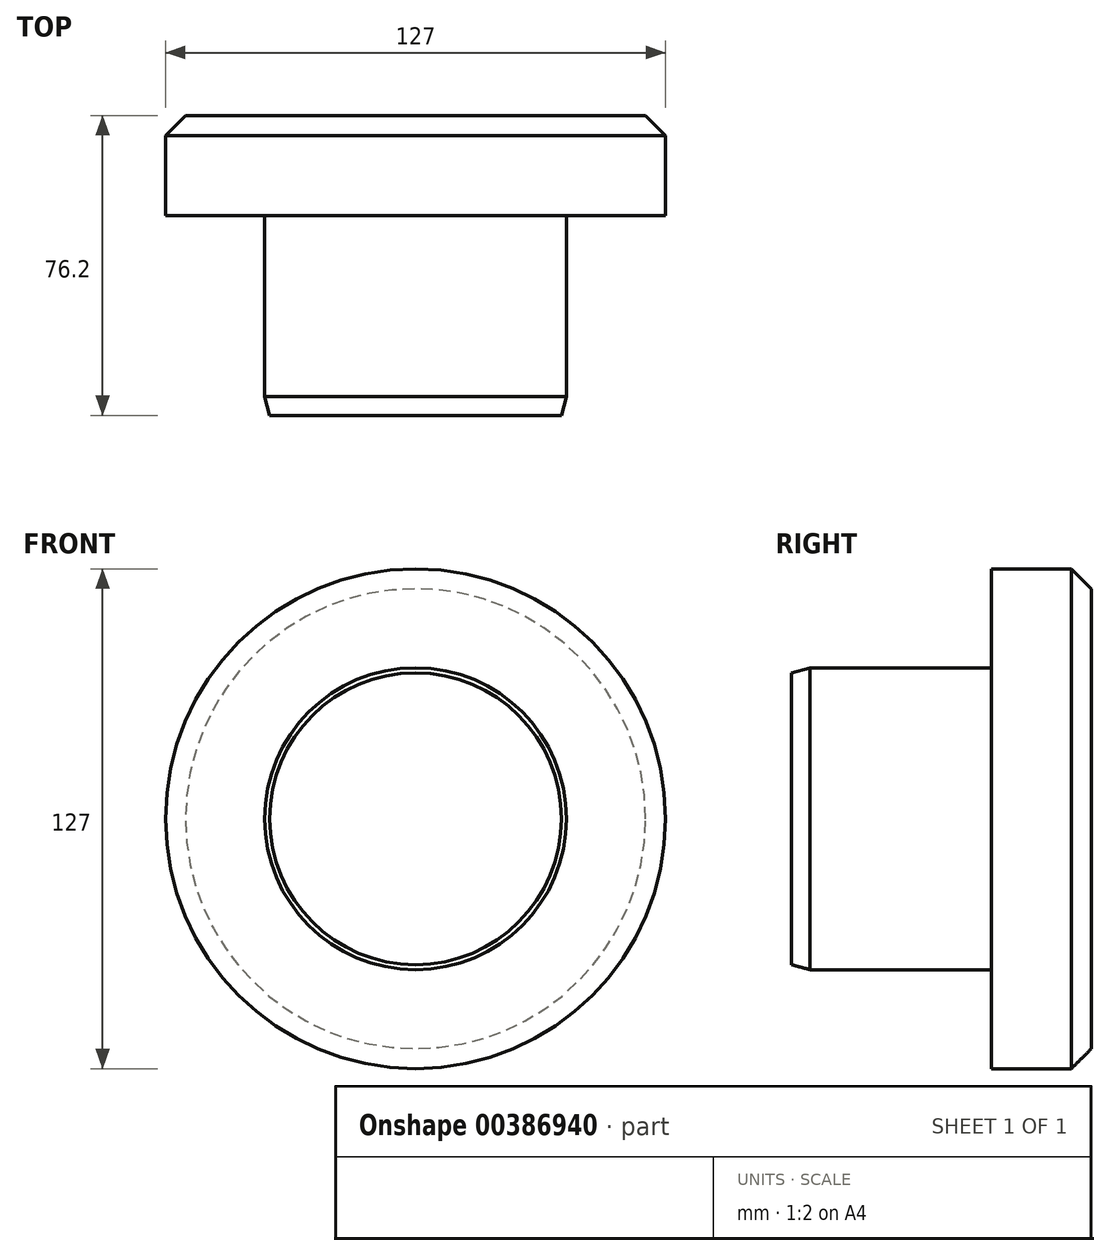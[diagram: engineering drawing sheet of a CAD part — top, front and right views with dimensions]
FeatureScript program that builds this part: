
annotation { "Feature Type Name" : "Feature", "Feature Type Description" : "" }
export const myFeature = defineFeature(function(context is Context, id is Id, definition is map)
    precondition{}
    {
        {
            var Q0;
            Q0=qCreatedBy(makeId("Front.planeOp"),FACE);
            var sketch = newSketch(context, id + "F0", { "sketchPlane" : qUnion([Q0])});
            skCircle(sketch, "E0", {"center": v(0, 0) * mm, "radius": 63.5 * mm});
            skSolve(sketch);
        }
        {
            var Q0;
            Q0 = qSketchRegion(id + "F0", true);
            extrude(context, id + "F1", {"entities" : qUnion([Q0]), "depth" : 76.2 * mm});
        }
        {
            var Q0;
            Q0=makeQuery(id+"F1.opExtrude","CAP_FACE",FACE,{"disambiguationData":[OSD([sQuery(id+"F0.wireOp",EDGE,"E0")])],"isStart":false});
            var sketch = newSketch(context, id + "F2", { "sketchPlane" : qUnion([Q0])});
            skCircle(sketch, "E1", {"center": v(0, 0) * mm, "radius": 38.35 * mm});
            skSolve(sketch);
        }
        {
            var Q0;
            Q0=makeQuery(id+"F2.imprint","IMPRINT",FACE,{"disambiguationData":[TD([[makeQuery(id+"F2.imprint","IMPRINT",EDGE,{"derivedFrom":sQuery(id+"F2.wireOp",EDGE,"E1")}),-1.0]])]});
            extrude(context, id + "F3", {"entities" : qUnion([Q0]), "operationType" : NewBodyOperationType.REMOVE, "oppositeDirection" : true, "depth" : 50.8 * mm});
        }
        {
            var Q0;
            Q0=makeQuery(id+"F3.boolean.opBoolean","COPY",EDGE,{"derivedFrom":makeQuery(id+"F3.opExtrude","CAP_EDGE",EDGE,{"disambiguationData":[OSD([sQuery(id+"F2.wireOp",EDGE,"E1")])],"isStart":true})});
            var Q1;
            Q1=makeQuery(id+"F1.opExtrude","CAP_FACE",FACE,{"disambiguationData":[OSD([sQuery(id+"F0.wireOp",EDGE,"E0")])],"isStart":false});
            chamfer(context, id + "F4", {"entities" : qUnion([Q0, Q1]), "chamferType" : ChamferType.OFFSET_ANGLE, "width" : 1.27 * mm, "oppositeDirection" : false, "angle" : 75 * degree, "tangentPropagation" : true});
        }
        {
            var Q0;
            Q0=makeQuery(id+"F1.opExtrude","CAP_EDGE",EDGE,{"disambiguationData":[OSD([sQuery(id+"F0.wireOp",EDGE,"E0")])],"isStart":true});
            chamfer(context, id + "F5", {"entities" : qUnion([Q0]), "width" : 5.08 * mm, "tangentPropagation" : true});
        }
    });
